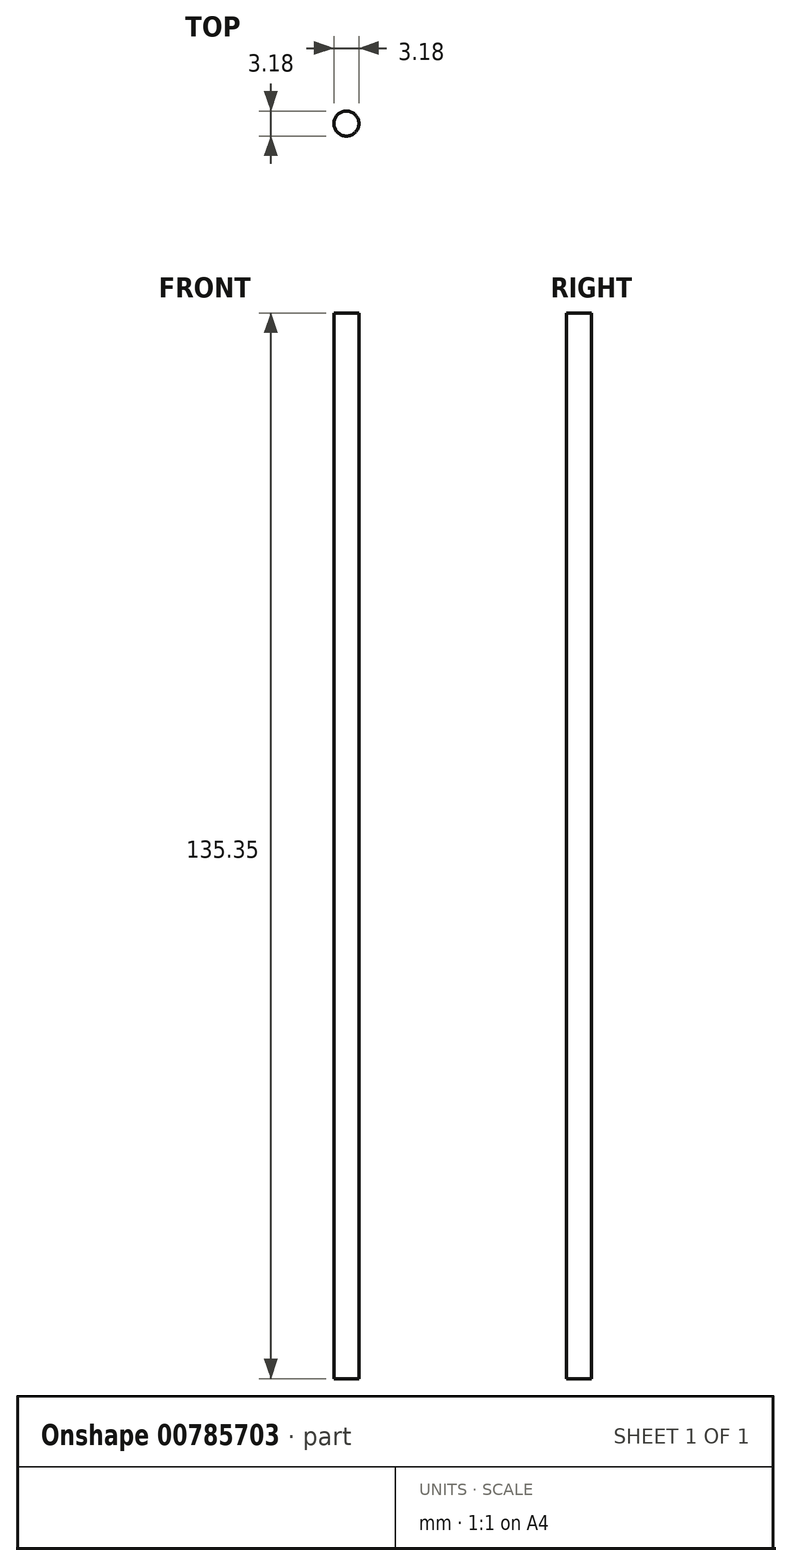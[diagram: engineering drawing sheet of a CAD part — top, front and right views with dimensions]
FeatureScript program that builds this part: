
annotation { "Feature Type Name" : "Feature", "Feature Type Description" : "" }
export const myFeature = defineFeature(function(context is Context, id is Id, definition is map)
    precondition{}
    {
        {
            var Q0;
            Q0=qCreatedBy(makeId("Top.planeOp"),FACE);
            var sketch = newSketch(context, id + "F0", { "sketchPlane" : qUnion([Q0])});
            skCircle(sketch, "E0", {"center": v(0, 0) * mm, "radius": 1.59 * mm});
            skSolve(sketch);
        }
        {
            var Q0;
            Q0 = qSketchRegion(id + "F0", true);
            extrude(context, id + "F1", {"entities" : qUnion([Q0]), "depth" : 135.35 * mm, "offsetDistance" : 25.4 * mm});
        }
    });
